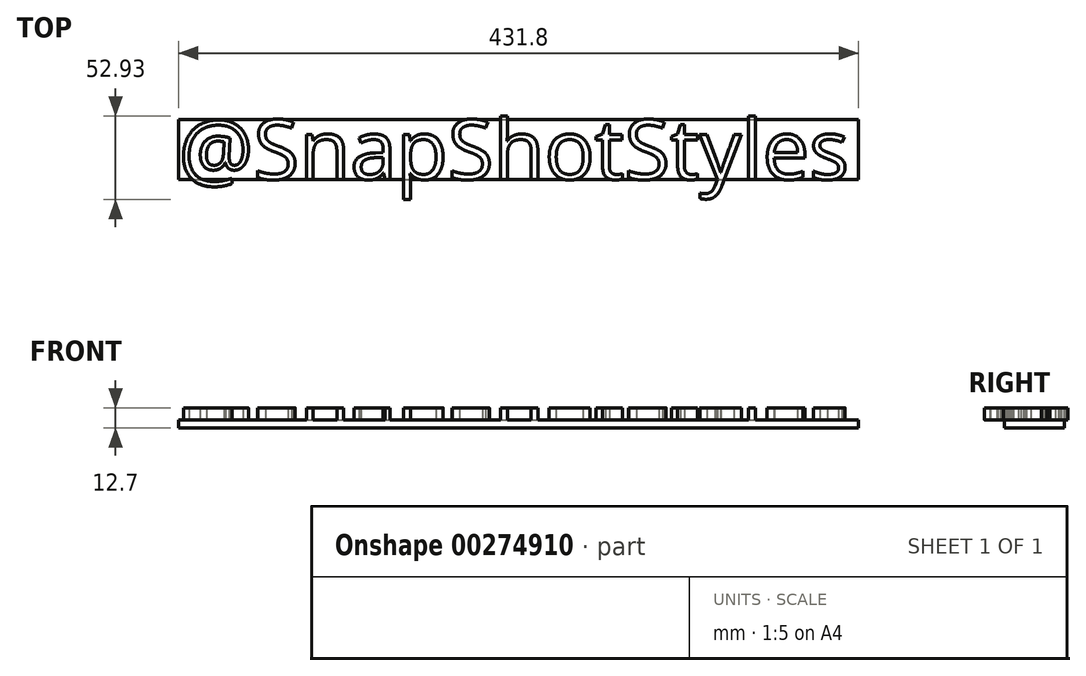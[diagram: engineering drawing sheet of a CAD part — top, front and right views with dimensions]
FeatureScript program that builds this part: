
annotation { "Feature Type Name" : "Feature", "Feature Type Description" : "" }
export const myFeature = defineFeature(function(context is Context, id is Id, definition is map)
    precondition{}
    {
        {
            var Q0;
            Q0=qCreatedBy(makeId("Top.planeOp"),FACE);
            var sketch = newSketch(context, id + "F0", { "sketchPlane" : qUnion([Q0])});
            skLineSegment(sketch, "E0.bottom", {"start": v(-29.28, 22.2) * mm, "end": v(402.52, 22.2) * mm});
            skLineSegment(sketch, "E0.top", {"start": v(-29.28, -15.9) * mm, "end": v(402.52, -15.9) * mm});
            skLineSegment(sketch, "E0.left", {"start": v(-29.28, 22.2) * mm, "end": v(-29.28, -15.9) * mm});
            skLineSegment(sketch, "E0.right", {"start": v(402.52, 22.2) * mm, "end": v(402.52, -15.9) * mm});
            skSolve(sketch);
        }
        {
            var Q0;
            Q0=makeQuery(id+"F0.imprint","IMPRINT",FACE,{"disambiguationData":[TD([[makeQuery(id+"F0.imprint","IMPRINT",EDGE,{"derivedFrom":sQuery(id+"F0.wireOp",EDGE,"E0.bottom")}),-1.0]])]});
            extrude(context, id + "F1", {"entities" : qUnion([Q0]), "depth" : 5.08 * mm});
        }
        {
            var Q0;
            Q0=makeQuery(id+"F1.opExtrude","CAP_FACE",FACE,{"disambiguationData":[OSD([sQuery(id+"F0.wireOp",EDGE,"E0.bottom"),sQuery(id+"F0.wireOp",EDGE,"E0.top"),sQuery(id+"F0.wireOp",EDGE,"E0.left"),sQuery(id+"F0.wireOp",EDGE,"E0.right")])],"isStart":false});
            var sketch = newSketch(context, id + "F2", { "sketchPlane" : qUnion([Q0])});
            skText(sketch, "E1", { "text": "@SnapShotStyles", "fontName": "OpenSans-Regular.ttf"});
            const initialGuessF2  = {"E1": [-0.02928, -0.0159, 1, 0, 0.0381]};
            skSetInitialGuess(sketch, initialGuessF2);
            skSolve(sketch);
        }
        {
            var Q0;
            Q0 = qSketchRegion(id + "F2", true);
            extrude(context, id + "F3", {"entities" : qUnion([Q0]), "operationType" : NewBodyOperationType.ADD, "depth" : 7.62 * mm});
        }
    });
